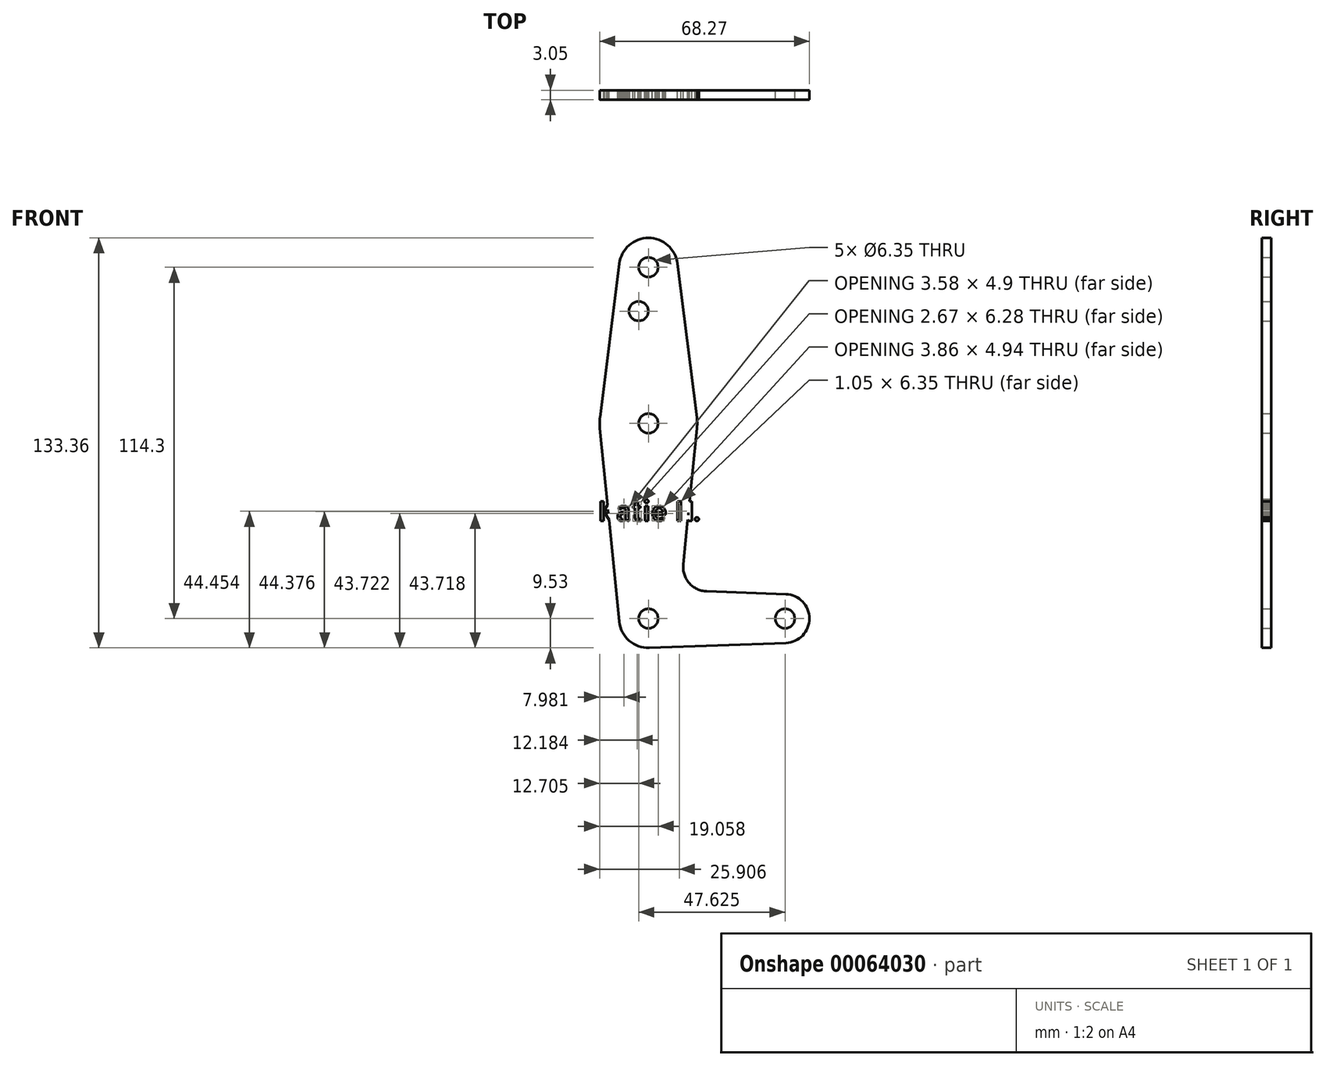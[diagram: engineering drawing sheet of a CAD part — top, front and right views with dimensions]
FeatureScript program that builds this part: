
annotation { "Feature Type Name" : "Feature", "Feature Type Description" : "" }
export const myFeature = defineFeature(function(context is Context, id is Id, definition is map)
    precondition{}
    {
        {
            var Q0;
            Q0=qCreatedBy(makeId("Front.planeOp"),FACE);
            var sketch = newSketch(context, id + "F0", { "sketchPlane" : qUnion([Q0])});
            skLineSegment(sketch, "E0", {"start": v(0, 114.3) * mm, "end": v(0, 0) * mm, "construction": true});
            skLineSegment(sketch, "E1", {"start": v(0, 0) * mm, "end": v(44.45, 0) * mm, "construction": true});
            skCircle(sketch, "E2", {"center": v(0, 114.3) * mm, "radius": 9.53 * mm});
            skCircle(sketch, "E3", {"center": v(0, 63.5) * mm, "radius": 15.88 * mm});
            skCircle(sketch, "E4", {"center": v(0, 0) * mm, "radius": 9.53 * mm});
            skCircle(sketch, "E5", {"center": v(44.45, 0) * mm, "radius": 7.94 * mm});
            skLineSegment(sketch, "E6", {"start": v(-9.45, 115.5) * mm, "end": v(-15.75, 65.48) * mm});
            skLineSegment(sketch, "E7", {"start": v(9.45, 115.5) * mm, "end": v(15.75, 65.48) * mm});
            skLineSegment(sketch, "E8", {"start": v(-15.8, 61.91) * mm, "end": v(-9.48, -0.95) * mm});
            skLineSegment(sketch, "E9", {"start": v(15.8, 61.91) * mm, "end": v(11.34, 17.6) * mm});
            skLineSegment(sketch, "E10", {"start": v(18.97, 8.85) * mm, "end": v(44.73, 7.93) * mm});
            skLineSegment(sketch, "E11", {"start": v(0.34, -9.52) * mm, "end": v(44.73, -7.93) * mm});
            skCircle(sketch, "E12", {"center": v(0, 114.3) * mm, "radius": 3.18 * mm});
            skCircle(sketch, "E13", {"center": v(0, 63.5) * mm, "radius": 3.18 * mm});
            skCircle(sketch, "E14", {"center": v(0, 0) * mm, "radius": 3.18 * mm});
            skCircle(sketch, "E15", {"center": v(44.45, 0) * mm, "radius": 3.18 * mm});
            skCircle(sketch, "E16", {"center": v(-3.18, 100.03) * mm, "radius": 3.18 * mm});
            skArc(sketch, "E17.filletArc", {"start": v(11.34, 17.6) * mm, "mid": v(13.26, 11.57) * mm, "end": v(18.97, 8.85) * mm});
            skText(sketch, "E18", { "text": "Katie N.", "fontName": "AllertaStencil-Regular.ttf"});
            const initialGuessF0  = {"E18": [-0.0164, 0.03175, 1, 0, 0.00635]};
            skSetInitialGuess(sketch, initialGuessF0);
            skSolve(sketch);
        }
        {
            var Q0;
            Q0 = qSketchRegion(id + "F0", true);
            extrude(context, id + "F1", {"entities" : qUnion([Q0]), "depth" : 3.05 * mm});
        }
    });
